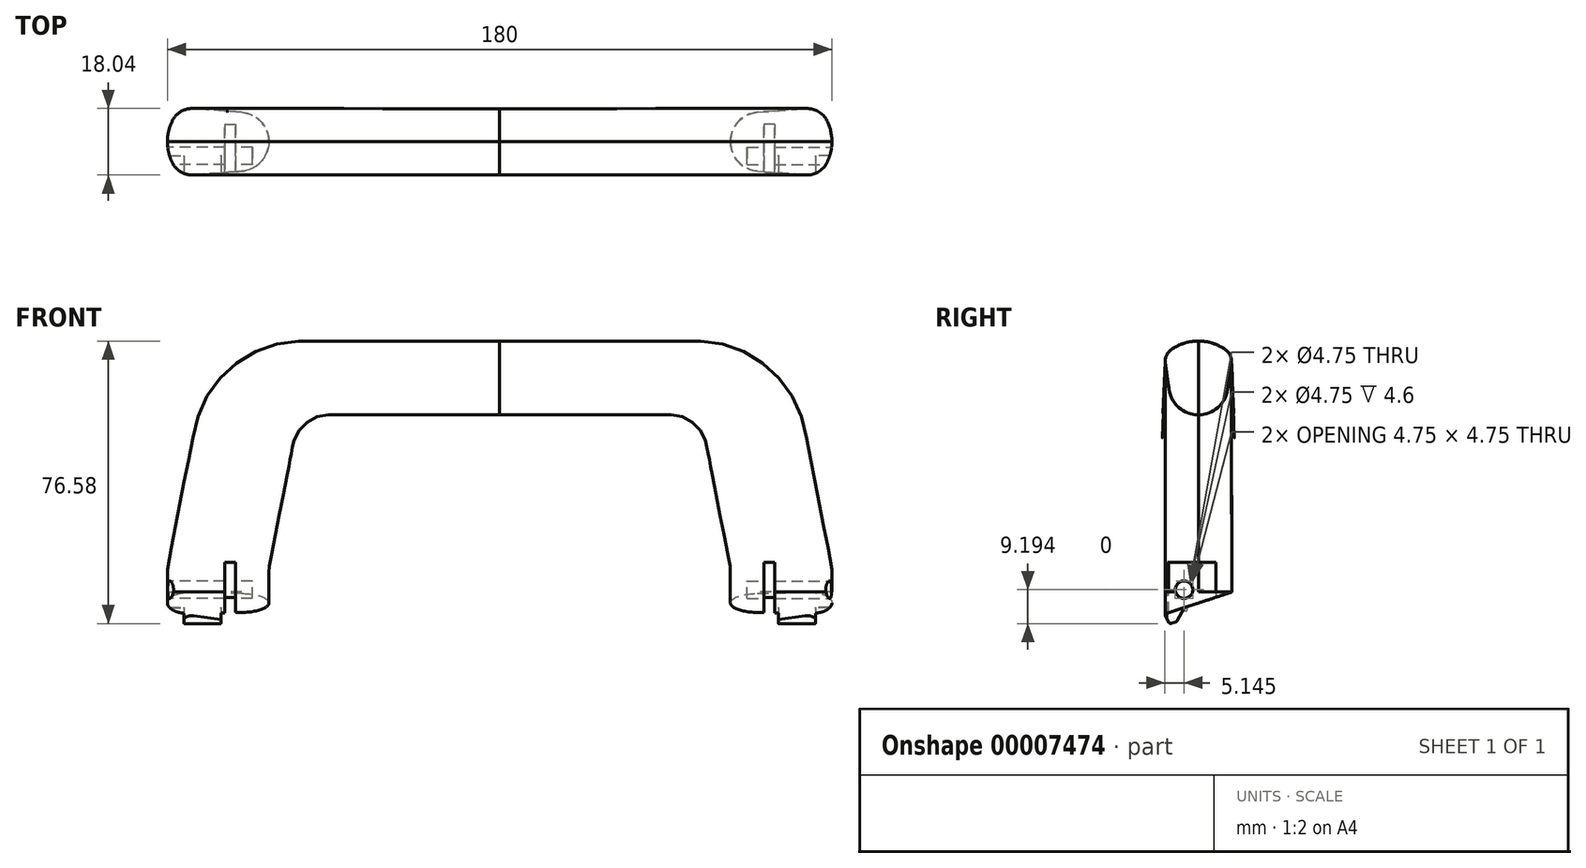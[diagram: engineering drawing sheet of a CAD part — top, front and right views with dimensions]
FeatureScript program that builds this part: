
annotation { "Feature Type Name" : "Feature", "Feature Type Description" : "" }
export const myFeature = defineFeature(function(context is Context, id is Id, definition is map)
    precondition{}
    {
        {
            var Q0;
            Q0=qCreatedBy(makeId("Front.planeOp"),FACE);
            var sketch = newSketch(context, id + "F0", { "sketchPlane" : qUnion([Q0])});
            skLineSegment(sketch, "E0.bottom", {"start": v(0, 68) * mm, "end": v(90, 68) * mm, "construction": true});
            skLineSegment(sketch, "E0.top", {"start": v(0, 0) * mm, "end": v(90, 0) * mm, "construction": true});
            skLineSegment(sketch, "E0.left", {"start": v(0, 68) * mm, "end": v(0, 0) * mm, "construction": true});
            skLineSegment(sketch, "E0.right", {"start": v(90, 68) * mm, "end": v(90, 0) * mm, "construction": true});
            skSolve(sketch);
        }
        {
            var Q0;
            Q0=qCreatedBy(makeId("Right.planeOp"),FACE);
            var sketch = newSketch(context, id + "F1", { "sketchPlane" : qUnion([Q0])});
            skArc(sketch, "E1", {"start": v(0, 48) * mm, "mid": v(5.23, 49.95) * mm, "end": v(7.92, 54.85) * mm});
            skArc(sketch, "E2", {"start": v(7.27, 65.71) * mm, "mid": v(3.81, 67.41) * mm, "end": v(0, 68) * mm});
            skLineSegment(sketch, "E3.rect.bottom", {"start": v(9.25, 48) * mm, "end": v(-9.25, 48) * mm, "construction": true});
            skLineSegment(sketch, "E3.rect.top", {"start": v(9.25, 68) * mm, "end": v(-9.25, 68) * mm, "construction": true});
            skLineSegment(sketch, "E3.rect.left", {"start": v(9.25, 48) * mm, "end": v(9.25, 68) * mm, "construction": true});
            skLineSegment(sketch, "E3.rect.right", {"start": v(-9.25, 48) * mm, "end": v(-9.25, 68) * mm, "construction": true});
            skPoint(sketch, "E3.rect.middle", {"position": v(0, 58) * mm});
            skPoint(sketch, "E4", {"position": v(9.25, 64) * mm});
            skLineSegment(sketch, "E5", {"start": v(8.94, 61.86) * mm, "end": v(7.92, 54.85) * mm});
            skLineSegment(sketch, "E6", {"start": v(0, 68) * mm, "end": v(0, 42.6) * mm, "construction": true});
            skArc(sketch, "E7.filletArc", {"start": v(8.94, 61.86) * mm, "mid": v(8.65, 64.02) * mm, "end": v(7.27, 65.71) * mm});
            skArc(sketch, "E8.0.MirrorCS", {"start": v(-7.27, 65.71) * mm, "mid": v(-3.81, 67.41) * mm, "end": v(0, 68) * mm});
            skArc(sketch, "E9.0.MirrorCS", {"start": v(-8.94, 61.86) * mm, "mid": v(-8.65, 64.02) * mm, "end": v(-7.27, 65.71) * mm});
            skLineSegment(sketch, "E10.0.MirrorCS", {"start": v(-8.94, 61.86) * mm, "end": v(-7.92, 54.85) * mm});
            skArc(sketch, "E11.0.MirrorCS", {"start": v(0, 48) * mm, "mid": v(-5.23, 49.95) * mm, "end": v(-7.92, 54.85) * mm});
            skSolve(sketch);
        }
        {
            var Q0;
            Q0=qCreatedBy(makeId("Top.planeOp"),FACE);
            var sketch = newSketch(context, id + "F2", { "sketchPlane" : qUnion([Q0])});
            skLineSegment(sketch, "E12.rect.bottom", {"start": v(90, -9.25) * mm, "end": v(62.5, -9.25) * mm, "construction": true});
            skLineSegment(sketch, "E12.rect.top", {"start": v(90, 9.25) * mm, "end": v(62.5, 9.25) * mm, "construction": true});
            skLineSegment(sketch, "E12.rect.left", {"start": v(90, -9.25) * mm, "end": v(90, 9.25) * mm, "construction": true});
            skLineSegment(sketch, "E12.rect.right", {"start": v(62.5, -9.25) * mm, "end": v(62.5, 9.25) * mm, "construction": true});
            skPoint(sketch, "E12.rect.middle", {"position": v(76.25, 0) * mm});
            skArc(sketch, "E13", {"start": v(69.87, 7.98) * mm, "mid": v(64.62, 5.43) * mm, "end": v(62.5, 0) * mm});
            skPoint(sketch, "E14", {"position": v(86, 9.25) * mm});
            skLineSegment(sketch, "E15", {"start": v(62.5, 0) * mm, "end": v(90, 0) * mm, "construction": true});
            skLineSegment(sketch, "E16", {"start": v(82.8, 9) * mm, "end": v(69.87, 7.98) * mm});
            skArc(sketch, "E17.trimOffspring", {"start": v(90, 0) * mm, "mid": v(89.65, 2.94) * mm, "end": v(88.64, 5.72) * mm});
            skPoint(sketch, "E18.center.orphan", {"position": v(139.87, 0) * mm});
            skArc(sketch, "E19.filletArc", {"start": v(88.64, 5.72) * mm, "mid": v(86.22, 8.25) * mm, "end": v(82.8, 9) * mm});
            skArc(sketch, "E20.0.MirrorCS", {"start": v(69.87, -7.98) * mm, "mid": v(64.62, -5.43) * mm, "end": v(62.5, 0) * mm});
            skLineSegment(sketch, "E21.0.MirrorCS", {"start": v(82.8, -9) * mm, "end": v(69.87, -7.98) * mm});
            skArc(sketch, "E22.0.MirrorCS", {"start": v(88.64, -5.72) * mm, "mid": v(86.22, -8.25) * mm, "end": v(82.8, -9) * mm});
            skArc(sketch, "E23.0.MirrorCS", {"start": v(90, 0) * mm, "mid": v(89.65, -2.94) * mm, "end": v(88.64, -5.72) * mm});
            skSolve(sketch);
        }
        {
            var Q0;
            Q0=qCreatedBy(makeId("Front.planeOp"),FACE);
            var sketch = newSketch(context, id + "F3", { "sketchPlane" : qUnion([Q0])});
            skLineSegment(sketch, "E24", {"start": v(0, 68) * mm, "end": v(53.29, 68) * mm});
            skLineSegment(sketch, "E25", {"start": v(82.73, 43.75) * mm, "end": v(89.81, 7.45) * mm});
            skLineSegment(sketch, "E26", {"start": v(90, 5.53) * mm, "end": v(90, 0) * mm});
            skPoint(sketch, "E27.visualSharp", {"position": v(78, 68) * mm});
            skArc(sketch, "E27.filletArc", {"start": v(82.73, 43.75) * mm, "mid": v(72.36, 61.16) * mm, "end": v(53.29, 68) * mm});
            skPoint(sketch, "E28.visualSharp", {"position": v(90, 6.5) * mm});
            skArc(sketch, "E28.filletArc", {"start": v(90, 5.53) * mm, "mid": v(89.95, 6.5) * mm, "end": v(89.81, 7.45) * mm});
            skSolve(sketch);
        }
        {
            var Q0;
            Q0=qCreatedBy(makeId("Front.planeOp"),FACE);
            var sketch = newSketch(context, id + "F4", { "sketchPlane" : qUnion([Q0])});
            skLineSegment(sketch, "E29", {"start": v(0, 48) * mm, "end": v(46.17, 48) * mm});
            skLineSegment(sketch, "E30", {"start": v(55.98, 39.92) * mm, "end": v(62.31, 7.45) * mm});
            skLineSegment(sketch, "E31", {"start": v(62.5, 5.53) * mm, "end": v(62.5, 0) * mm});
            skPoint(sketch, "E32.visualSharp", {"position": v(54.4, 48) * mm});
            skArc(sketch, "E32.filletArc", {"start": v(55.98, 39.92) * mm, "mid": v(52.52, 45.72) * mm, "end": v(46.17, 48) * mm});
            skPoint(sketch, "E33.visualSharp", {"position": v(62.5, 6.5) * mm});
            skArc(sketch, "E33.filletArc", {"start": v(62.5, 5.53) * mm, "mid": v(62.45, 6.5) * mm, "end": v(62.31, 7.45) * mm});
            skSolve(sketch);
        }
        {
            var Q0;
            Q0 = qSketchRegion(id + "F1", true);
            var Q1;
            Q1 = qSketchRegion(id + "F2", true);
            var Q2;
            Q2 = qBodyType(qCreatedBy(id + "F3" ,EDGE), BodyType.WIRE);
            var Q3;
            Q3 = qBodyType(qCreatedBy(id + "F4" ,EDGE), BodyType.WIRE);
            loft(context, id + "F5", {"addGuides" : true, "sheetProfilesArray" : [{ "sheetProfileEntities" : qUnion([Q0]) }, { "sheetProfileEntities" : qUnion([Q1]) }], "guidesArray" : [{ "guideEntities" : qUnion([Q2]), "guideDerivativeType" : LoftGuideDerivativeType.DEFAULT, "guideDerivativeMagnitude" : 1 }, { "guideEntities" : qUnion([Q3]), "guideDerivativeType" : LoftGuideDerivativeType.DEFAULT, "guideDerivativeMagnitude" : 1 }]});
        }
        {
            var Q0;
            Q0=makeQuery(id+"F5.opLoft","CAP_FACE",FACE,{"disambiguationData":[OSD([makeQuery(id+"F2.imprint","IMPRINT",FACE,{"disambiguationData":[TD([[makeQuery(id+"F2.imprint","IMPRINT",EDGE,{"derivedFrom":sQuery(id+"F2.wireOp",EDGE,"E13")}),1.0]])]})])],"isStart":true});
            extrude(context, id + "F6", {"entities" : qUnion([Q0]), "operationType" : NewBodyOperationType.ADD, "depth" : 10 * mm});
        }
        {
            var Q0;
            Q0=qCreatedBy(makeId("Right.planeOp"),FACE);
            var sketch = newSketch(context, id + "F7", { "sketchPlane" : qUnion([Q0])});
            skLineSegment(sketch, "E34", {"start": v(9.25, 0) * mm, "end": v(-3.78, -4.23) * mm});
            skLineSegment(sketch, "E35", {"start": v(-9.25, -6.01) * mm, "end": v(-9.25, -10) * mm});
            skLineSegment(sketch, "E36", {"start": v(-9.25, -10) * mm, "end": v(9.25, -10) * mm});
            skLineSegment(sketch, "E37", {"start": v(9.25, -10) * mm, "end": v(9.25, 0) * mm});
            skLineSegment(sketch, "E38", {"start": v(9.25, 0) * mm, "end": v(-9.25, 0) * mm, "construction": true});
            skLineSegment(sketch, "E39", {"start": v(-9.25, -6.01) * mm, "end": v(-7.75, -8.68) * mm});
            skLineSegment(sketch, "E40", {"start": v(-7.75, -8.68) * mm, "end": v(-5.85, -8.06) * mm});
            skLineSegment(sketch, "E41", {"start": v(-5.85, -8.06) * mm, "end": v(-3.78, -4.23) * mm});
            skSolve(sketch);
        }
        {
            var Q0;
            Q0 = qSketchRegion(id + "F7", true);
            extrude(context, id + "F8", {"entities" : qUnion([Q0]), "operationType" : NewBodyOperationType.REMOVE, "endBound" : BoundingType.THROUGH_ALL, "depth" : 25 * mm});
        }
        {
            var Q0;
            Q0=qCreatedBy(makeId("Front.planeOp"),FACE);
            var Q1;
            Q1=sQuery(id+"F2.wireOp",VERTEX,"E12.rect.left.start");
            cPlane(context, id + "F9", {"entities" : qUnion([Q0, Q1]), "cplaneType" : CPlaneType.PLANE_POINT, "offset" : 150 * mm, "width" : 150 * mm, "height" : 150 * mm});
        }
        {
            var Q0;
            Q0=qCreatedBy(id+"F9.planeOp",FACE);
            var sketch = newSketch(context, id + "F10", { "sketchPlane" : qUnion([Q0])});
            skLineSegment(sketch, "E42.bottom", {"start": v(71.6, 7.99) * mm, "end": v(74.5, 7.99) * mm});
            skLineSegment(sketch, "E42.top", {"start": v(71.6, -6.01) * mm, "end": v(74.5, -6.01) * mm});
            skLineSegment(sketch, "E42.left", {"start": v(71.6, 7.99) * mm, "end": v(71.6, -6.01) * mm});
            skLineSegment(sketch, "E42.right", {"start": v(74.5, 7.99) * mm, "end": v(74.5, -6.01) * mm});
            skSolve(sketch);
        }
        {
            var Q0;
            Q0 = qSketchRegion(id + "F10", true);
            extrude(context, id + "F11", {"entities" : qUnion([Q0]), "operationType" : NewBodyOperationType.REMOVE, "oppositeDirection" : true, "depth" : 14 * mm});
        }
        {
            var Q0;
            Q0=makeQuery(id+"F11.boolean.opBoolean","COPY",FACE,{"derivedFrom":makeQuery(id+"F11.opExtrude","SWEPT_FACE",FACE,{"disambiguationData":[OSD([sQuery(id+"F10.wireOp",EDGE,"E42.right")])]})});
            cPlane(context, id + "F12", {"entities" : qUnion([Q0]), "cplaneType" : CPlaneType.OFFSET, "offset" : 1 * mm, "oppositeDirection" : true, "width" : 150 * mm, "height" : 150 * mm});
        }
        {
            var Q0;
            Q0=qCreatedBy(id+"F12.planeOp",FACE);
            var sketch = newSketch(context, id + "F13", { "sketchPlane" : qUnion([Q0])});
            skLineSegment(sketch, "E43", {"start": v(3.78, -4.23) * mm, "end": v(9.25, -6.01) * mm});
            skLineSegment(sketch, "E44", {"start": v(9.25, -6.01) * mm, "end": v(9.25, -10) * mm});
            skLineSegment(sketch, "E45", {"start": v(9.25, -10) * mm, "end": v(3.78, -10) * mm});
            skLineSegment(sketch, "E46", {"start": v(3.78, -10) * mm, "end": v(3.78, -4.23) * mm});
            skSolve(sketch);
        }
        {
            var Q0;
            Q0 = qSketchRegion(id + "F13", true);
            extrude(context, id + "F14", {"entities" : qUnion([Q0]), "operationType" : NewBodyOperationType.REMOVE, "endBound" : BoundingType.THROUGH_ALL, "depth" : 25 * mm});
        }
        {
            var Q0;
            Q0=makeQuery(id+"F8.boolean.opBoolean","COPY",EDGE,{"derivedFrom":makeQuery(id+"F8.opExtrude","SWEPT_EDGE",EDGE,{"disambiguationData":[OSD([sQuery(id+"F7.wireOp",EDGE,"E39"),sQuery(id+"F7.wireOp",EDGE,"E40")])]})});
            var Q1;
            Q1=makeQuery(id+"F8.boolean.opBoolean","COPY",EDGE,{"derivedFrom":makeQuery(id+"F8.opExtrude","SWEPT_EDGE",EDGE,{"disambiguationData":[OSD([sQuery(id+"F7.wireOp",EDGE,"E40"),sQuery(id+"F7.wireOp",EDGE,"E41")])]})});
            var Q2;
            {var subQ0=sQuery(id+"F7.wireOp",EDGE,"E34");var subQ1=sQuery(id+"F7.wireOp",EDGE,"E41");Q2=makeQuery(id+"F11.boolean.opBoolean","SPLIT",EDGE,{"disambiguationData":[TD([makeQuery(id+"F11.opExtrude","SWEPT_FACE",FACE,{"disambiguationData":[OSD([sQuery(id+"F10.wireOp",EDGE,"E42.right")])]})])],"derivedFrom":makeQuery(id+"F8.boolean.opBoolean","COPY",EDGE,{"derivedFrom":makeQuery(id+"F8.opExtrude","SWEPT_EDGE",EDGE,{"disambiguationData":[OSD([subQ0,subQ1])]})})});}
            fillet(context, id + "F15", {"entities" : qUnion([Q0, Q1, Q2]), "radius" : 0.5 * mm, "tangentPropagation" : true, "allowEdgeOverflow" : false});
        }
        {
            var Q0;
            Q0=qCreatedBy(id+"F12.planeOp",FACE);
            cPlane(context, id + "F16", {"entities" : qUnion([Q0]), "cplaneType" : CPlaneType.OFFSET, "offset" : 10 * mm, "oppositeDirection" : true, "width" : 150 * mm, "height" : 150 * mm});
        }
        {
            var Q0;
            Q0=qCreatedBy(id+"F16.planeOp",FACE);
            var sketch = newSketch(context, id + "F17", { "sketchPlane" : qUnion([Q0])});
            skLineSegment(sketch, "E47.0", {"start": v(3.78, -4.23) * mm, "end": v(9.25, -6.01) * mm});
            skLineSegment(sketch, "E47.1", {"start": v(9.25, -6.01) * mm, "end": v(9.25, -10) * mm});
            skLineSegment(sketch, "E47.2", {"start": v(9.25, -10) * mm, "end": v(3.78, -10) * mm});
            skLineSegment(sketch, "E47.3", {"start": v(3.78, -10) * mm, "end": v(3.78, -4.23) * mm});
            skSolve(sketch);
        }
        {
            var Q0;
            Q0 = qSketchRegion(id + "F17", true);
            extrude(context, id + "F18", {"entities" : qUnion([Q0]), "operationType" : NewBodyOperationType.REMOVE, "endBound" : BoundingType.THROUGH_ALL, "oppositeDirection" : true, "depth" : 25 * mm});
        }
        {
            var Q0;
            Q0=qCreatedBy(makeId("Right.planeOp"),FACE);
            var Q1;
            Q1=sQuery(id+"F0.wireOp",VERTEX,"E0.bottom.end");
            cPlane(context, id + "F19", {"entities" : qUnion([Q0, Q1]), "cplaneType" : CPlaneType.PLANE_POINT, "offset" : 150 * mm, "width" : 150 * mm, "height" : 150 * mm});
        }
        {
            var Q0;
            Q0=qCreatedBy(id+"F19.planeOp",FACE);
            var sketch = newSketch(context, id + "F20", { "sketchPlane" : qUnion([Q0])});
            skCircle(sketch, "E48", {"center": v(-3.87, 0.61) * mm, "radius": 2.38 * mm});
            skLineSegment(sketch, "E49", {"start": v(-12, 2.99) * mm, "end": v(7.12, 2.99) * mm, "construction": true});
            skLineSegment(sketch, "E50", {"start": v(-6.25, 2.99) * mm, "end": v(-6.25, -15.29) * mm, "construction": true});
            skSolve(sketch);
        }
        {
            var Q0;
            Q0 = qSketchRegion(id + "F20", true);
            extrude(context, id + "F21", {"entities" : qUnion([Q0]), "operationType" : NewBodyOperationType.REMOVE, "oppositeDirection" : true, "depth" : 23 * mm});
        }
        {
            var Q0;
            Q0=makeQuery(id+"F5.opLoft","SWEPT_BODY",BODY,{"disambiguationData":[OSD([makeQuery(id+"F1.imprint","IMPRINT",FACE,{"disambiguationData":[TD([[makeQuery(id+"F1.imprint","IMPRINT",EDGE,{"derivedFrom":sQuery(id+"F1.wireOp",EDGE,"E1")}),1.0]])]}),makeQuery(id+"F2.imprint","IMPRINT",FACE,{"disambiguationData":[TD([[makeQuery(id+"F2.imprint","IMPRINT",EDGE,{"derivedFrom":sQuery(id+"F2.wireOp",EDGE,"E13")}),1.0]])]}),sQuery(id+"F3.wireOp",EDGE,"E24"),sQuery(id+"F4.wireOp",EDGE,"E29")])]});
            var Q1;
            Q1=qCreatedBy(makeId("Right.planeOp"),FACE);
            mirror(context, id + "F22", {"entities" : qUnion([Q0]), "mirrorPlane" : qUnion([Q1])});
        }
    });
